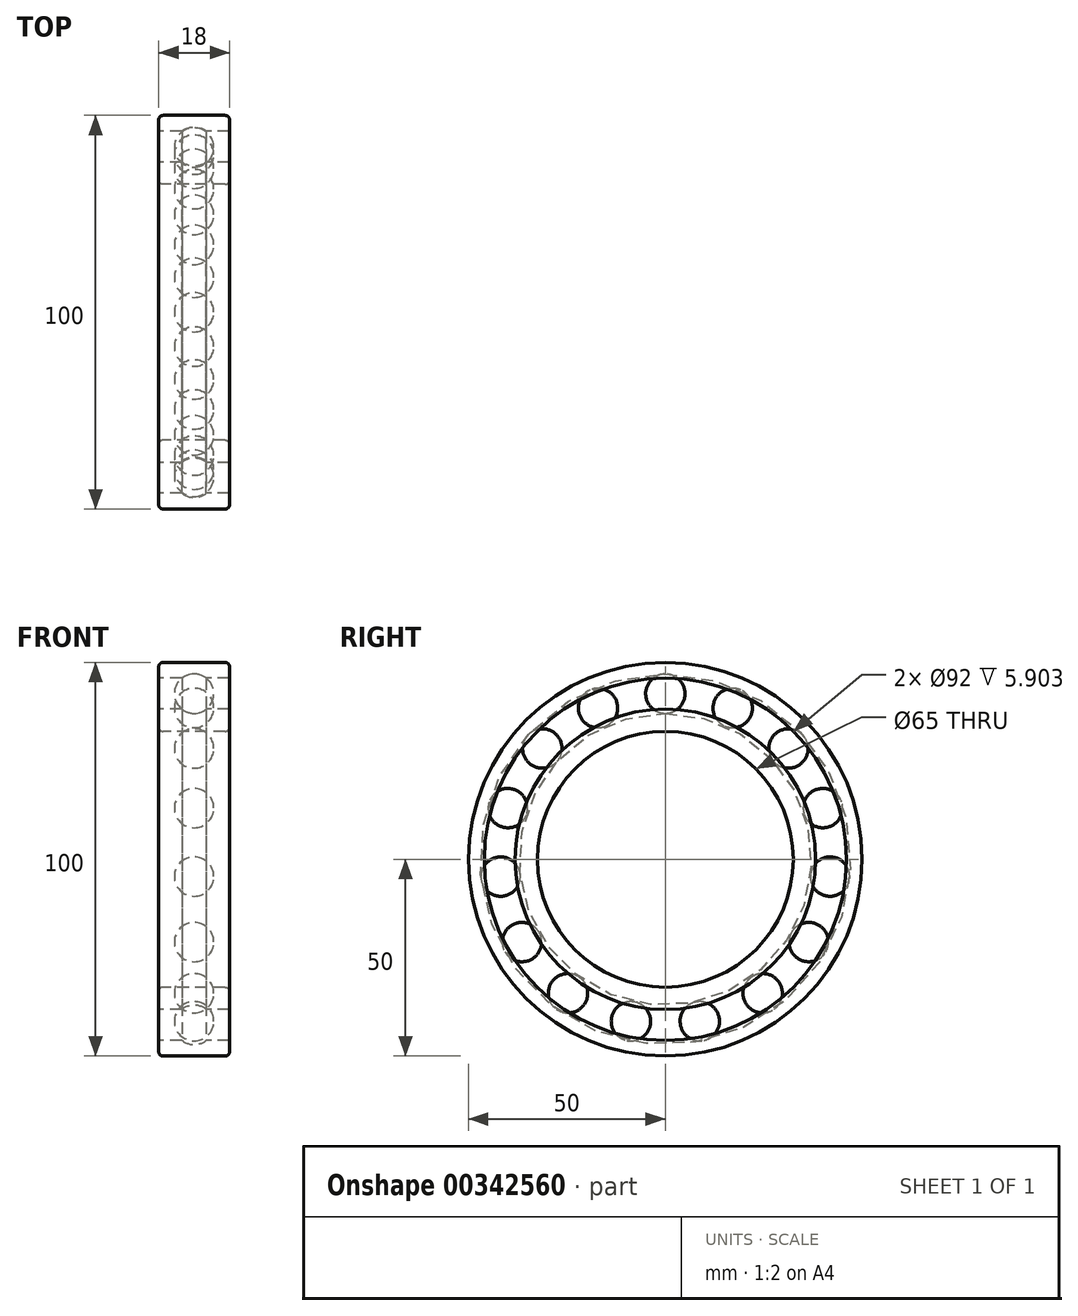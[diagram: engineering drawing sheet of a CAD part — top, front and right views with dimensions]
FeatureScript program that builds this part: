
annotation { "Feature Type Name" : "Feature", "Feature Type Description" : "" }
export const myFeature = defineFeature(function(context is Context, id is Id, definition is map)
    precondition{}
    {
        {
            var Q0;
            Q0=qCreatedBy(makeId("Front.planeOp"),FACE);
            var sketch = newSketch(context, id + "F0", { "sketchPlane" : qUnion([Q0])});
            skLineSegment(sketch, "E0", {"start": v(9, 33.6) * mm, "end": v(9, 38.15) * mm});
            skLineSegment(sketch, "E1", {"start": v(9, 38.15) * mm, "end": v(3.1, 38.15) * mm});
            skLineSegment(sketch, "E2", {"start": v(-9, 38.15) * mm, "end": v(-9, 33.6) * mm});
            skLineSegment(sketch, "E3", {"start": v(-7.9, 32.5) * mm, "end": v(7.9, 32.5) * mm});
            skPoint(sketch, "E4.visualSharp", {"position": v(-9, 32.5) * mm});
            skArc(sketch, "E4.filletArc", {"start": v(-9, 33.6) * mm, "mid": v(-8.68, 32.82) * mm, "end": v(-7.9, 32.5) * mm});
            skPoint(sketch, "E5.visualSharp", {"position": v(9, 32.5) * mm});
            skArc(sketch, "E5.filletArc", {"start": v(7.9, 32.5) * mm, "mid": v(8.68, 32.82) * mm, "end": v(9, 33.6) * mm});
            skLineSegment(sketch, "E6", {"start": v(0, 37.08) * mm, "end": v(0, 47.07) * mm});
            skPoint(sketch, "E6.endSnap0", {"position": v(0, 38.15) * mm});
            skLineSegment(sketch, "E7", {"start": v(3.1, 46) * mm, "end": v(9, 46) * mm});
            skLineSegment(sketch, "E8", {"start": v(9, 46) * mm, "end": v(9, 48.9) * mm});
            skLineSegment(sketch, "E9", {"start": v(7.9, 50) * mm, "end": v(-7.9, 50) * mm});
            skLineSegment(sketch, "E10", {"start": v(-9, 48.9) * mm, "end": v(-9, 46) * mm});
            skLineSegment(sketch, "E11", {"start": v(-9, 46) * mm, "end": v(-3.1, 46) * mm});
            skPoint(sketch, "E12.orphan", {"position": v(0, 32.5) * mm});
            skArc(sketch, "E13", {"start": v(-3.1, 38.15) * mm, "mid": v(5, 42.07) * mm, "end": v(-3.1, 46) * mm});
            skLineSegment(sketch, "E14.trimOffspring", {"start": v(-3.1, 38.15) * mm, "end": v(-9, 38.15) * mm});
            skPoint(sketch, "E15.orphan", {"position": v(0, 46) * mm});
            skPoint(sketch, "E16.visualSharp", {"position": v(-9, 50) * mm});
            skArc(sketch, "E16.filletArc", {"start": v(-7.9, 50) * mm, "mid": v(-8.68, 49.68) * mm, "end": v(-9, 48.9) * mm});
            skPoint(sketch, "E17.visualSharp", {"position": v(9, 50) * mm});
            skArc(sketch, "E17.filletArc", {"start": v(9, 48.9) * mm, "mid": v(8.68, 49.68) * mm, "end": v(7.9, 50) * mm});
            skLineSegment(sketch, "E18", {"start": v(-13, 0) * mm, "end": v(16.63, 0) * mm});
            skSolve(sketch);
        }
        {
            var Q0;
            Q0=makeQuery(id+"F0.imprint","IMPRINT",FACE,{"disambiguationData":[TD([[makeQuery(id+"F0.imprint","IMPRINT",EDGE,{"derivedFrom":sQuery(id+"F0.wireOp",EDGE,"E0")}),1.0]])]});
            var Q1;
            {var subQ0=sQuery(id+"F0.wireOp",EDGE,"E7");Q1=makeQuery(id+"F0.imprint","IMPRINT",FACE,{"disambiguationData":[TD([[makeQuery(id+"F0.imprint","IMPRINT",EDGE,{"derivedFrom":subQ0}),1.0]])]});}
            var Q2;
            Q2=sQuery(id+"F0.wireOp",EDGE,"E18");
            revolve(context, id + "F1", {"entities" : qUnion([Q0, Q1]), "axis" : qUnion([Q2]), "revolveType" : RevolveType.FULL});
        }
        {
            var Q0;
            {var subQ0=sQuery(id+"F0.wireOp",EDGE,"E6");Q0=makeQuery(id+"F0.imprint","IMPRINT",FACE,{"disambiguationData":[TD([[makeQuery(id+"F0.imprint","IMPRINT",EDGE,{"derivedFrom":subQ0}),-1.0]])]});}
            var Q1;
            Q1=sQuery(id+"F0.wireOp",EDGE,"E6");
            revolve(context, id + "F2", {"entities" : qUnion([Q0]), "axis" : qUnion([Q1]), "revolveType" : RevolveType.FULL});
        }
        {
            var Q0;
            Q0=makeQuery(id+"F2.opRevolve","SWEPT_BODY",BODY,{"disambiguationData":[OSD([sQuery(id+"F0.wireOp",EDGE,"E6"),sQuery(id+"F0.wireOp",EDGE,"E13")])]});
            var Q1;
            Q1=sQuery(id+"F0.wireOp",EDGE,"E18");
            circularPattern(context, id + "F3", {"entities" : qUnion([Q0]), "axis" : qUnion([Q1]), "angle" : 360 * degree, "instanceCount" : 15, "equalSpace" : true});
        }
    });
